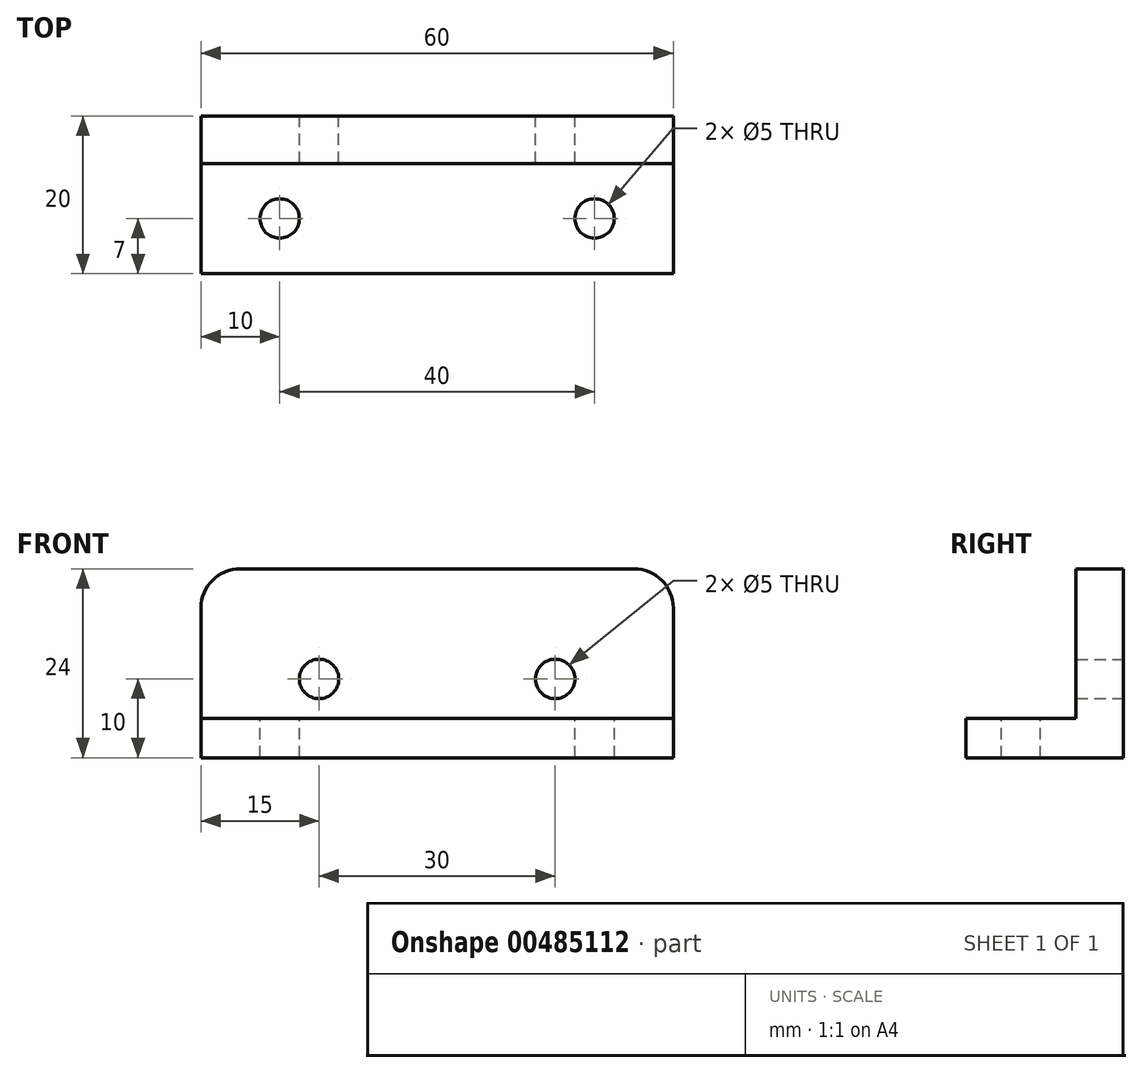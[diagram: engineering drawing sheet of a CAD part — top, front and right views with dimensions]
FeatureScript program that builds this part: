
annotation { "Feature Type Name" : "Feature", "Feature Type Description" : "" }
export const myFeature = defineFeature(function(context is Context, id is Id, definition is map)
    precondition{}
    {
        {
            var Q0;
            Q0=qCreatedBy(makeId("Front.planeOp"),FACE);
            var sketch = newSketch(context, id + "F0", { "sketchPlane" : qUnion([Q0])});
            skLineSegment(sketch, "E0.bottom", {"start": v(-30, 12) * mm, "end": v(30, 12) * mm});
            skLineSegment(sketch, "E0.top", {"start": v(-30, -12) * mm, "end": v(30, -12) * mm});
            skLineSegment(sketch, "E0.left", {"start": v(-30, 12) * mm, "end": v(-30, -12) * mm});
            skLineSegment(sketch, "E0.right", {"start": v(30, 12) * mm, "end": v(30, -12) * mm});
            skPoint(sketch, "E0.middle", {"position": v(0, 0) * mm});
            skLineSegment(sketch, "E1", {"start": v(-15, 12) * mm, "end": v(-15, -12) * mm, "construction": true});
            skLineSegment(sketch, "E2", {"start": v(15, 12) * mm, "end": v(15, -12) * mm, "construction": true});
            skLineSegment(sketch, "E3", {"start": v(-30, -2) * mm, "end": v(30, -2) * mm, "construction": true});
            skCircle(sketch, "E4", {"center": v(-15, -2) * mm, "radius": 2.5 * mm});
            skCircle(sketch, "E5", {"center": v(15, -2) * mm, "radius": 2.5 * mm});
            skLineSegment(sketch, "E6", {"start": v(-30, -7) * mm, "end": v(30, -7) * mm});
            skSolve(sketch);
        }
        {
            var Q0;
            {var subQ1=sQuery(id+"F0.wireOp",EDGE,"E0.bottom");Q0=makeQuery(id+"F0.imprint","IMPRINT",FACE,{"disambiguationData":[TD([[makeQuery(id+"F0.imprint","IMPRINT",EDGE,{"derivedFrom":subQ1}),-1.0]])]});}
            extrude(context, id + "F1", {"entities" : qUnion([Q0]), "depth" : 6 * mm, "offsetDistance" : 25 * mm});
        }
        {
            var Q0;
            {var subQ0=sQuery(id+"F0.wireOp",EDGE,"E0.top");Q0=makeQuery(id+"F0.imprint","IMPRINT",FACE,{"disambiguationData":[TD([[makeQuery(id+"F0.imprint","IMPRINT",EDGE,{"derivedFrom":subQ0}),1.0]])]});}
            extrude(context, id + "F2", {"entities" : qUnion([Q0]), "operationType" : NewBodyOperationType.ADD, "depth" : 20 * mm, "offsetDistance" : 25 * mm});
        }
        {
            var Q0;
            Q0=makeQuery(id+"F2.opExtrude","SWEPT_FACE",FACE,{"disambiguationData":[OSD([sQuery(id+"F0.wireOp",EDGE,"E6")])]});
            var sketch = newSketch(context, id + "F3", { "sketchPlane" : qUnion([Q0])});
            skLineSegment(sketch, "E7", {"start": v(-20, -6) * mm, "end": v(-20, -20) * mm, "construction": true});
            skLineSegment(sketch, "E8", {"start": v(20, -6) * mm, "end": v(20, -20) * mm, "construction": true});
            skLineSegment(sketch, "E9", {"start": v(-30, -13) * mm, "end": v(30, -13) * mm, "construction": true});
            skLineSegment(sketch, "E10.bottom", {"start": v(-30, -6) * mm, "end": v(30, -6) * mm, "construction": true});
            skLineSegment(sketch, "E10.top", {"start": v(-30, -20) * mm, "end": v(30, -20) * mm, "construction": true});
            skLineSegment(sketch, "E10.left", {"start": v(-30, -6) * mm, "end": v(-30, -20) * mm, "construction": true});
            skLineSegment(sketch, "E10.right", {"start": v(30, -6) * mm, "end": v(30, -20) * mm, "construction": true});
            skCircle(sketch, "E11", {"center": v(-20, -13) * mm, "radius": 2.5 * mm});
            skCircle(sketch, "E12", {"center": v(20, -13) * mm, "radius": 2.5 * mm});
            skLineSegment(sketch, "E13", {"start": v(29.92, 0) * mm, "end": v(30, -20) * mm, "construction": true});
            skSolve(sketch);
        }
        {
            var Q0;
            Q0=sQuery(id+"F3.wireOp",VERTEX,"E11.center");
            var Q1;
            Q1=sQuery(id+"F3.wireOp",VERTEX,"E12.center");
            var Q2;
            Q2=makeQuery(id+"F1.opExtrude","SWEPT_BODY",BODY,{"disambiguationData":[OSD([sQuery(id+"F0.wireOp",EDGE,"E0.bottom"),sQuery(id+"F0.wireOp",EDGE,"E0.left"),sQuery(id+"F0.wireOp",EDGE,"E0.right"),sQuery(id+"F0.wireOp",EDGE,"E4"),sQuery(id+"F0.wireOp",EDGE,"E5"),sQuery(id+"F0.wireOp",EDGE,"E6")])]});
            hole(context, id + "F4", {"style" : HoleStyle.SIMPLE, "endStyle" : HoleEndStyle.THROUGH, "holeDiameter" : 5 * mm, "isTappedThrough" : true, "tappedDepth" : 12 * mm, "tapClearance" : 3, "locations" : qUnion([Q0, Q1]), "scope" : qUnion([Q2])});
        }
        {
            var Q0;
            Q0=makeQuery(id+"F1.opExtrude","SWEPT_EDGE",EDGE,{"disambiguationData":[OSD([sQuery(id+"F0.wireOp",EDGE,"E0.bottom"),sQuery(id+"F0.wireOp",EDGE,"E0.left")])]});
            var Q1;
            Q1=makeQuery(id+"F1.opExtrude","SWEPT_EDGE",EDGE,{"disambiguationData":[OSD([sQuery(id+"F0.wireOp",EDGE,"E0.bottom"),sQuery(id+"F0.wireOp",EDGE,"E0.right")])]});
            fillet(context, id + "F5", {"entities" : qUnion([Q0, Q1]), "radius" : 5 * mm, "tangentPropagation" : true, "allowEdgeOverflow" : false});
        }
    });
